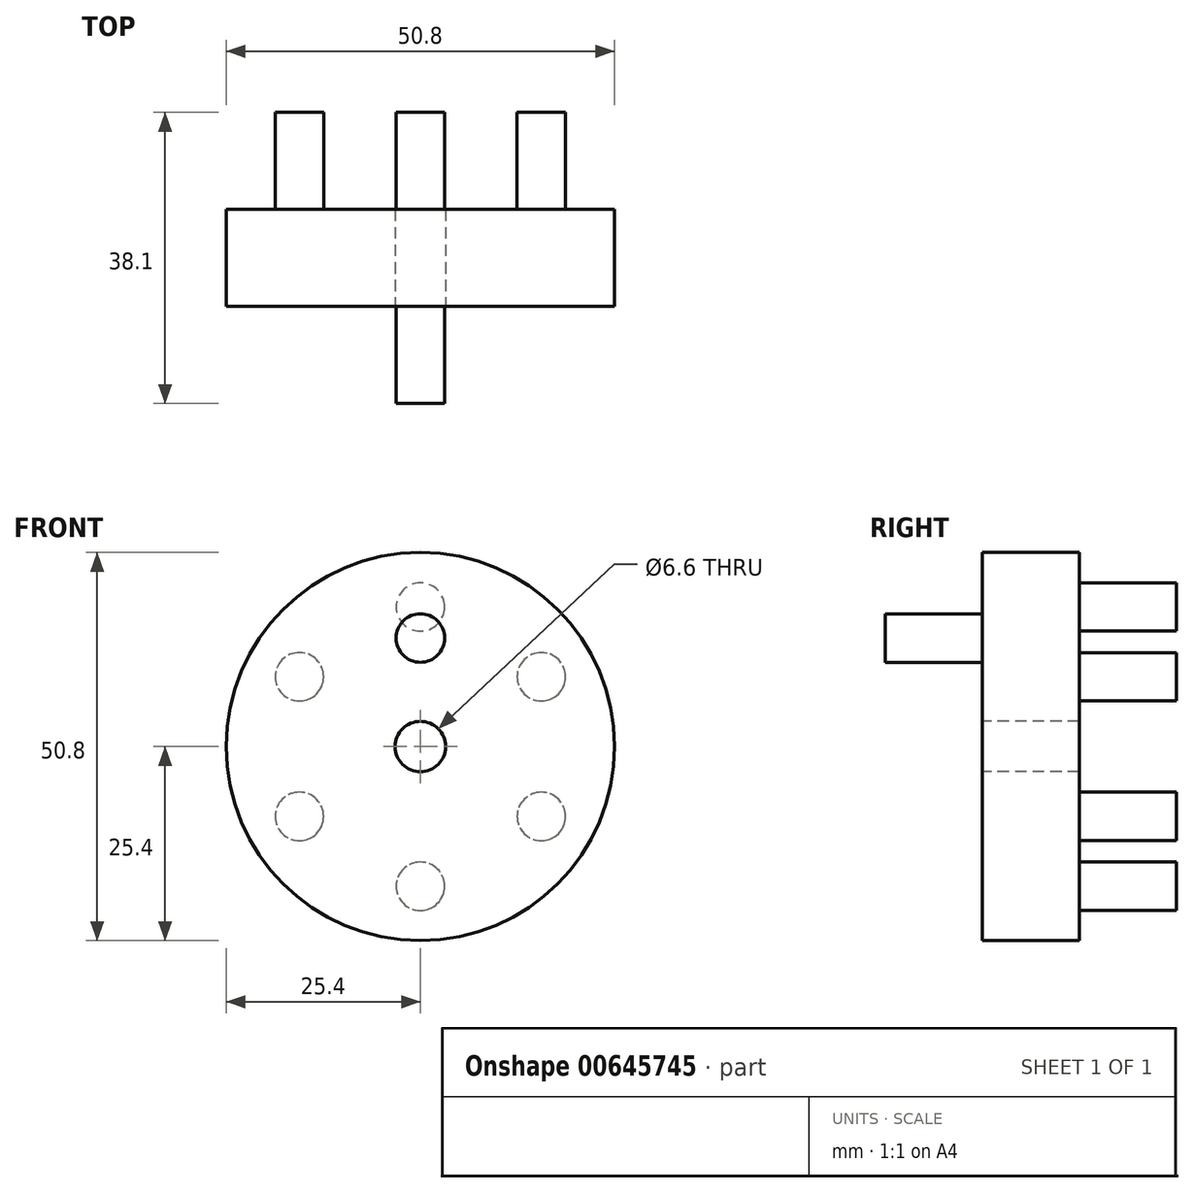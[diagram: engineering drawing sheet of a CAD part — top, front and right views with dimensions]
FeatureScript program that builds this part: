
annotation { "Feature Type Name" : "Feature", "Feature Type Description" : "" }
export const myFeature = defineFeature(function(context is Context, id is Id, definition is map)
    precondition{}
    {
        {
            var Q0;
            Q0=qCreatedBy(makeId("Front.planeOp"),FACE);
            var sketch = newSketch(context, id + "F0", { "sketchPlane" : qUnion([Q0])});
            skCircle(sketch, "E0", {"center": v(0, 0) * mm, "radius": 25.4 * mm});
            skSolve(sketch);
        }
        {
            var Q0;
            Q0 = qSketchRegion(id + "F0", true);
            extrude(context, id + "F1", {"entities" : qUnion([Q0]), "depth" : 12.7 * mm, "offsetDistance" : 25.4 * mm});
        }
        {
            var Q0;
            Q0=makeQuery(id+"F1.opExtrude","CAP_FACE",FACE,{"disambiguationData":[OSD([sQuery(id+"F0.wireOp",EDGE,"E0")])],"isStart":false});
            var sketch = newSketch(context, id + "F2", { "sketchPlane" : qUnion([Q0])});
            skCircle(sketch, "E1", {"center": v(0, 0) * mm, "radius": 3.3 * mm});
            skSolve(sketch);
        }
        {
            var Q0;
            Q0 = qSketchRegion(id + "F2", true);
            extrude(context, id + "F3", {"entities" : qUnion([Q0]), "operationType" : NewBodyOperationType.REMOVE, "oppositeDirection" : true, "depth" : 12.7 * mm, "offsetDistance" : 25.4 * mm});
        }
        {
            var Q0;
            Q0=makeQuery(id+"F1.opExtrude","CAP_FACE",FACE,{"disambiguationData":[OSD([sQuery(id+"F0.wireOp",EDGE,"E0")])],"isStart":false});
            var sketch = newSketch(context, id + "F4", { "sketchPlane" : qUnion([Q0])});
            skCircle(sketch, "E2", {"center": v(0, 14.21) * mm, "radius": 3.18 * mm});
            skSolve(sketch);
        }
        {
            var Q0;
            Q0 = qSketchRegion(id + "F4", true);
            extrude(context, id + "F5", {"entities" : qUnion([Q0]), "operationType" : NewBodyOperationType.ADD, "depth" : 12.7 * mm, "offsetDistance" : 25.4 * mm});
        }
        {
            var Q0;
            Q0=makeQuery(id+"F1.opExtrude","CAP_FACE",FACE,{"disambiguationData":[OSD([sQuery(id+"F0.wireOp",EDGE,"E0")])],"isStart":true});
            var sketch = newSketch(context, id + "F6", { "sketchPlane" : qUnion([Q0])});
            skCircle(sketch, "E3", {"center": v(0, 18.28) * mm, "radius": 3.17 * mm});
            skCircle(sketch, "E4.1.0", {"center": v(-15.83, 9.14) * mm, "radius": 3.17 * mm});
            skCircle(sketch, "E4.2.0", {"center": v(-15.83, -9.14) * mm, "radius": 3.17 * mm});
            skCircle(sketch, "E4.3.0", {"center": v(0, -18.28) * mm, "radius": 3.17 * mm});
            skCircle(sketch, "E4.4.0", {"center": v(15.83, -9.14) * mm, "radius": 3.17 * mm});
            skCircle(sketch, "E4.5.0", {"center": v(15.83, 9.14) * mm, "radius": 3.17 * mm});
            skPoint(sketch, "E4.center", {"position": v(0, 0) * mm});
            skSolve(sketch);
        }
        {
            var Q0;
            Q0 = qSketchRegion(id + "F6", true);
            extrude(context, id + "F7", {"entities" : qUnion([Q0]), "operationType" : NewBodyOperationType.ADD, "depth" : 12.7 * mm, "offsetDistance" : 25.4 * mm});
        }
    });
